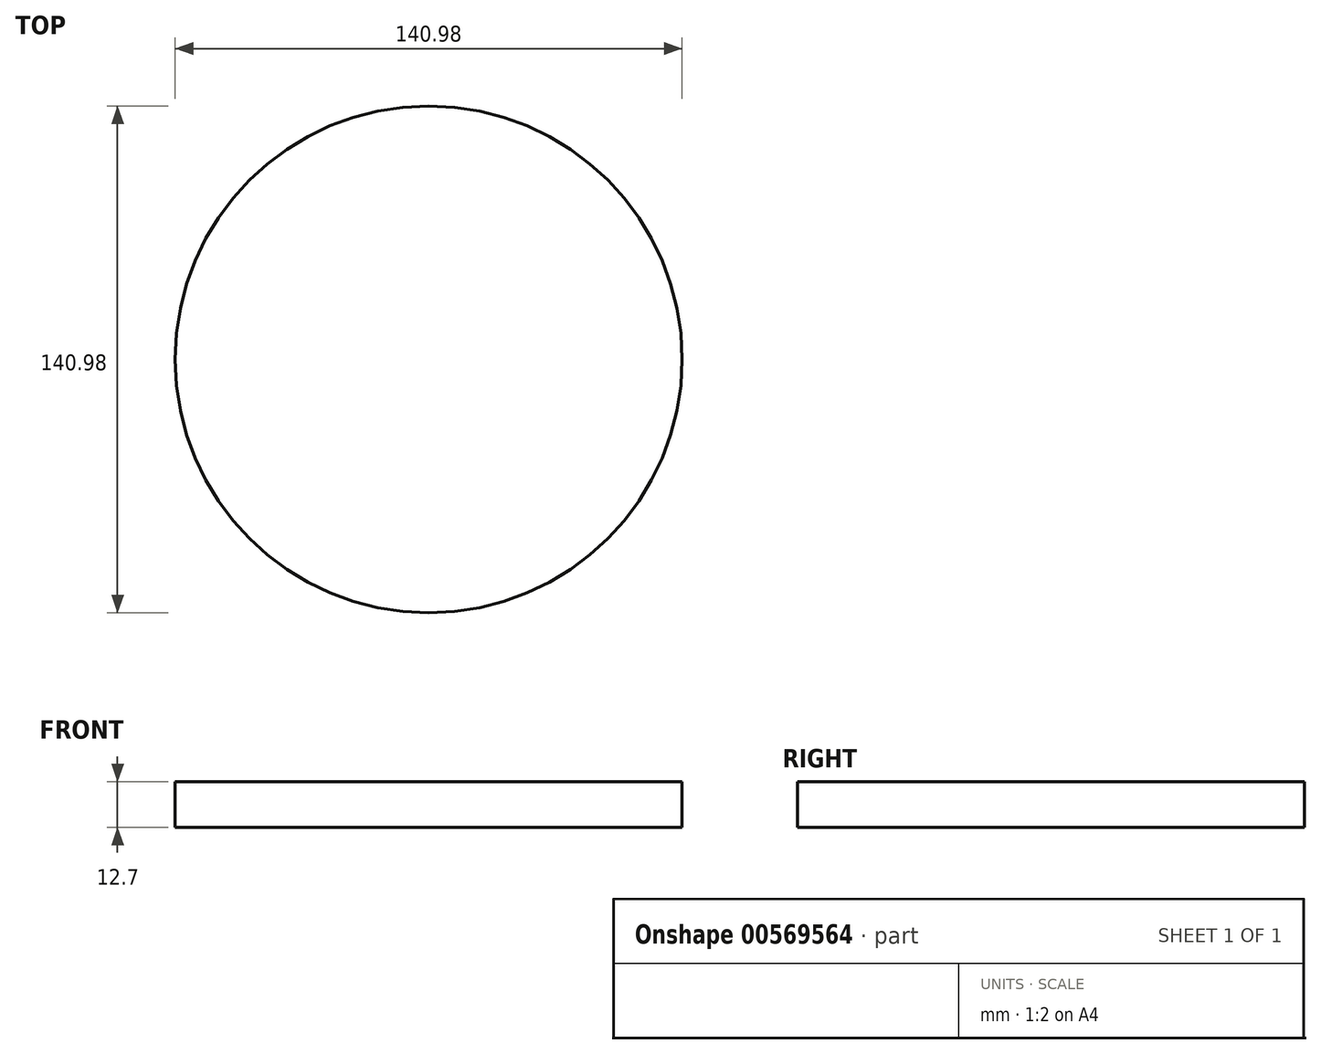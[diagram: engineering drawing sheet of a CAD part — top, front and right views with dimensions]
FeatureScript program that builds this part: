
annotation { "Feature Type Name" : "Feature", "Feature Type Description" : "" }
export const myFeature = defineFeature(function(context is Context, id is Id, definition is map)
    precondition{}
    {
        {
            var Q0;
            Q0=qCreatedBy(makeId("Top.planeOp"),FACE);
            var sketch = newSketch(context, id + "F0", { "sketchPlane" : qUnion([Q0])});
            skCircle(sketch, "E0", {"center": v(0, 0) * mm, "radius": 70.48 * mm});
            skSolve(sketch);
        }
        {
            var Q0;
            Q0 = qSketchRegion(id + "F0", true);
            extrude(context, id + "F1", {"entities" : qUnion([Q0]), "depth" : 12.7 * mm, "offsetDistance" : 25.4 * mm});
        }
    });
